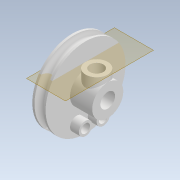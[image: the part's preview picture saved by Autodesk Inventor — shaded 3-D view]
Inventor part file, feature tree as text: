
AUTODESK INVENTOR PART (.ipt)
format: ipt  version: 2020.2 (Build 242310000, 310)  size: 210,944 bytes
history: native  units: mm
features: sketch x8, extrude x7, revolve x1, plane x1
ambient origin geometry x8: Origin, YZ Plane, XZ Plane, XY Plane, X Axis, Y Axis, Z Axis, Center Point
bodies: Solid1 (feature_tree)
feature tree (17):
  revolve  "Revolution1"  [1 undecoded]
  extrude  "Extrusion4"  Depth=1.5mm
  extrude  "Extrusion5"  Depth=6.0mm
  extrude  "Extrusion6"  Depth=9.0mm TaperAngle=0.0deg
  extrude  "Extrusion7"  Depth=2.0mm
  extrude  "Extrusion8"  Depth=3.0mm
  plane  "Work Plane1"
  extrude  "Extrusion9"  Depth=2.0mm
  extrude  "Extrusion10"  Depth=10.0mm TaperAngle=0.0deg
  sketch  "Sketch1"  dims[d0=9.0mm d1=2.0mm]
  sketch  "Sketch6"  dims[d2=1.5mm d3=1.5mm]
  sketch  "Sketch7"  dims[d4=90.0deg d14=6.0mm]
  sketch  "Sketch8"  dims[d15=2.0mm d16=9.0mm d17=0.0mm]
  sketch  "Sketch9"  dims[d18=2.0mm d19=2.0mm]
  sketch  "Sketch10"  dims[d20=3.0mm d21=3.0mm]
  sketch  "Sketch12"  dims[d22=2.0mm d23=0.0mm d24=2.0mm]
  sketch  "Sketch13"  dims[d25=2.0mm d26=10.0mm d27=0.0mm d28=7.0mm d29=5.0mm d30=0.0mm d31=3.3mm d32=0.0mm d33=0.0mm d35=5.0mm d36=5.0mm d37=10.0mm d38=0.0mm d39=3.0mm d40=10.0mm d41=0.0mm]
note: 1 required parameter value undecoded (feature->parameter linkage not recoverable at this tier; creation-order binding heuristic only, values carry confidence <= 0.55)
